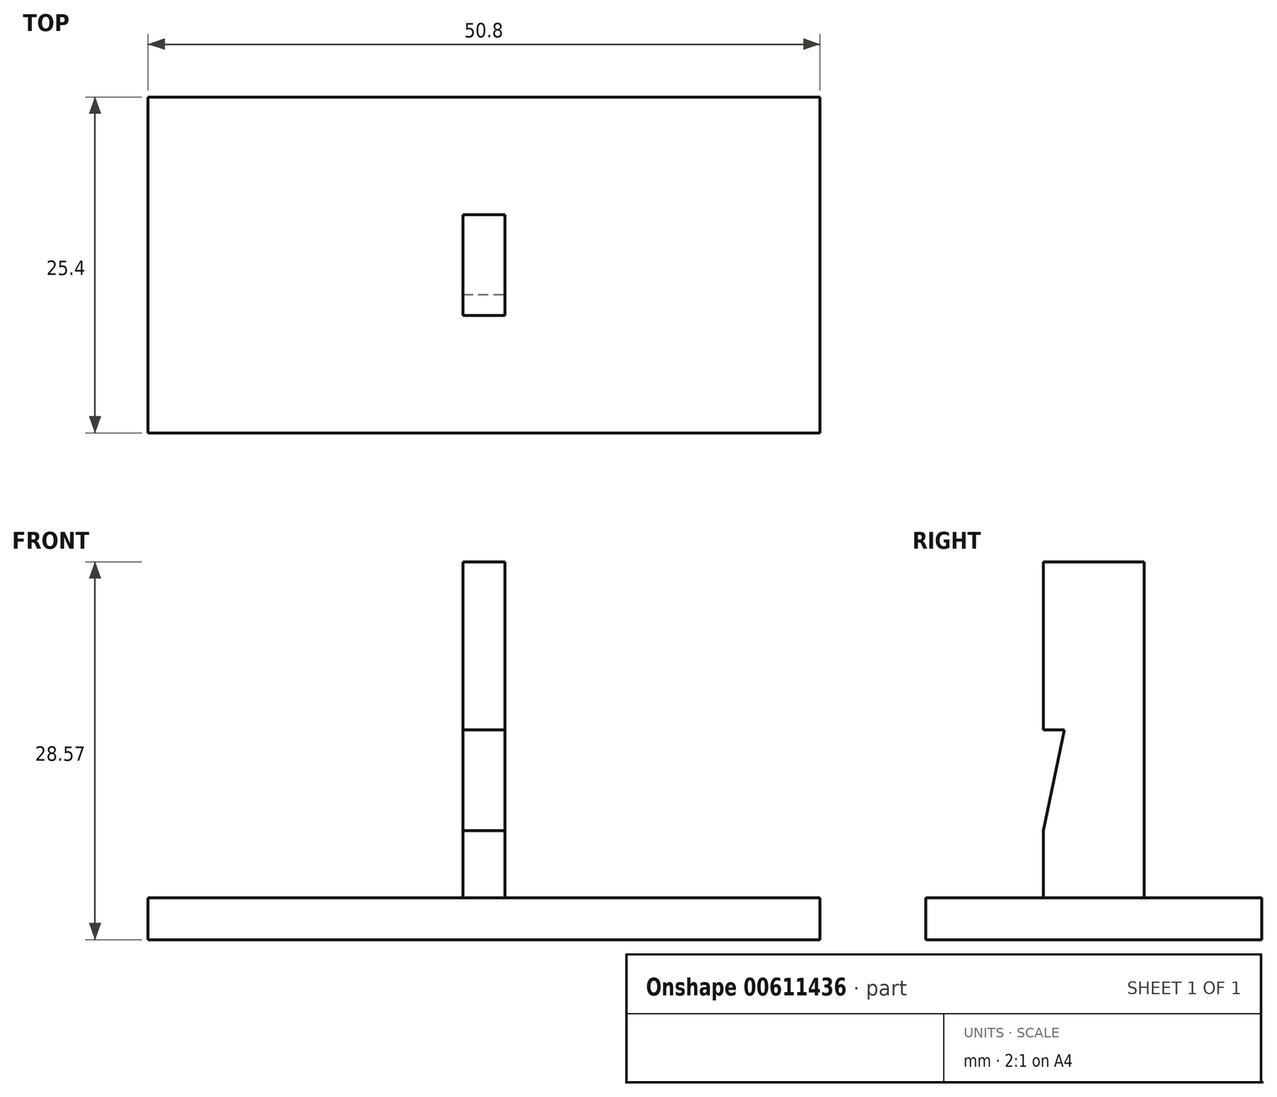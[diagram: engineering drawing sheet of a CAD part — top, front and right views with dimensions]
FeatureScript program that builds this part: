
annotation { "Feature Type Name" : "Feature", "Feature Type Description" : "" }
export const myFeature = defineFeature(function(context is Context, id is Id, definition is map)
    precondition{}
    {
        {
            var Q0;
            Q0=qCreatedBy(makeId("Top.planeOp"),FACE);
            var sketch = newSketch(context, id + "F0", { "sketchPlane" : qUnion([Q0])});
            skLineSegment(sketch, "E0.bottom", {"start": v(0, 0) * mm, "end": v(50.8, 0) * mm});
            skLineSegment(sketch, "E0.top", {"start": v(0, -25.4) * mm, "end": v(50.8, -25.4) * mm});
            skLineSegment(sketch, "E0.left", {"start": v(0, 0) * mm, "end": v(0, -25.4) * mm});
            skLineSegment(sketch, "E0.right", {"start": v(50.8, 0) * mm, "end": v(50.8, -25.4) * mm});
            skSolve(sketch);
        }
        {
            var Q0;
            Q0=makeQuery(id+"F0.imprint","IMPRINT",FACE,{"disambiguationData":[TD([[makeQuery(id+"F0.imprint","IMPRINT",EDGE,{"derivedFrom":sQuery(id+"F0.wireOp",EDGE,"E0.bottom")}),-1.0]])]});
            extrude(context, id + "F1", {"entities" : qUnion([Q0]), "depth" : 3.17 * mm, "offsetDistance" : 25.4 * mm});
        }
        {
            var Q0;
            Q0=makeQuery(id+"F1.opExtrude","CAP_FACE",FACE,{"disambiguationData":[OSD([sQuery(id+"F0.wireOp",EDGE,"E0.bottom"),sQuery(id+"F0.wireOp",EDGE,"E0.top"),sQuery(id+"F0.wireOp",EDGE,"E0.left"),sQuery(id+"F0.wireOp",EDGE,"E0.right")])],"isStart":false});
            var sketch = newSketch(context, id + "F2", { "sketchPlane" : qUnion([Q0])});
            skLineSegment(sketch, "E1", {"start": v(25.4, 0) * mm, "end": v(25.4, -25.4) * mm});
            skLineSegment(sketch, "E2", {"start": v(0, -12.7) * mm, "end": v(50.8, -12.7) * mm});
            skLineSegment(sketch, "E3", {"start": v(23.81, -12.7) * mm, "end": v(23.81, -16.51) * mm});
            skLineSegment(sketch, "E4", {"start": v(23.81, -16.51) * mm, "end": v(25.4, -16.51) * mm});
            skLineSegment(sketch, "E5.MirrorCS", {"start": v(23.81, -8.9) * mm, "end": v(25.4, -8.9) * mm});
            skLineSegment(sketch, "E6.MirrorCS", {"start": v(23.81, -12.7) * mm, "end": v(23.81, -8.9) * mm});
            skLineSegment(sketch, "E7.MirrorCS", {"start": v(26.99, -16.51) * mm, "end": v(25.4, -16.51) * mm});
            skLineSegment(sketch, "E8.MirrorCS", {"start": v(26.99, -12.7) * mm, "end": v(26.99, -16.51) * mm});
            skLineSegment(sketch, "E9.MirrorCS", {"start": v(26.99, -12.7) * mm, "end": v(26.99, -8.9) * mm});
            skLineSegment(sketch, "E10.MirrorCS", {"start": v(26.99, -8.9) * mm, "end": v(25.4, -8.9) * mm});
            skSolve(sketch);
        }
        {
            var Q0;
            {var subQ0=sQuery(id+"F2.wireOp",EDGE,"E7.MirrorCS");Q0=makeQuery(id+"F2.imprint","IMPRINT",FACE,{"disambiguationData":[TD([[makeQuery(id+"F2.imprint","IMPRINT",EDGE,{"derivedFrom":subQ0}),-1.0]])]});}
            var Q1;
            {var subQ4=sQuery(id+"F2.wireOp",EDGE,"E3");Q1=makeQuery(id+"F2.imprint","IMPRINT",FACE,{"disambiguationData":[TD([[makeQuery(id+"F2.imprint","IMPRINT",EDGE,{"derivedFrom":subQ4}),1.0]])]});}
            var Q2;
            {var subQ4=sQuery(id+"F2.wireOp",EDGE,"E9.MirrorCS");Q2=makeQuery(id+"F2.imprint","IMPRINT",FACE,{"disambiguationData":[TD([[makeQuery(id+"F2.imprint","IMPRINT",EDGE,{"derivedFrom":subQ4}),1.0]])]});}
            var Q3;
            {var subQ0=sQuery(id+"F2.wireOp",EDGE,"E5.MirrorCS");Q3=makeQuery(id+"F2.imprint","IMPRINT",FACE,{"disambiguationData":[TD([[makeQuery(id+"F2.imprint","IMPRINT",EDGE,{"derivedFrom":subQ0}),-1.0]])]});}
            extrude(context, id + "F3", {"entities" : qUnion([Q0, Q1, Q2, Q3]), "operationType" : NewBodyOperationType.ADD, "depth" : 25.4 * mm, "offsetDistance" : 25.4 * mm});
        }
        {
            var Q0;
            Q0=makeQuery(id+"F3.opExtrude","SWEPT_FACE",FACE,{"disambiguationData":[OSD([sQuery(id+"F2.wireOp",EDGE,"E8.MirrorCS"),sQuery(id+"F2.wireOp",EDGE,"E9.MirrorCS")])]});
            var sketch = newSketch(context, id + "F4", { "sketchPlane" : qUnion([Q0])});
            skLineSegment(sketch, "E11", {"start": v(-16.51, 15.88) * mm, "end": v(-14.92, 15.88) * mm});
            skLineSegment(sketch, "E12", {"start": v(-14.92, 15.88) * mm, "end": v(-16.51, 8.26) * mm});
            skLineSegment(sketch, "E13", {"start": v(-16.51, 15.88) * mm, "end": v(-16.51, 8.26) * mm});
            skSolve(sketch);
        }
        {
            var Q0;
            Q0=makeQuery(id+"F4.imprint","IMPRINT",FACE,{"disambiguationData":[TD([[makeQuery(id+"F4.imprint","IMPRINT",EDGE,{"derivedFrom":sQuery(id+"F4.wireOp",EDGE,"E11")}),-1.0]])]});
            extrude(context, id + "F5", {"entities" : qUnion([Q0]), "operationType" : NewBodyOperationType.REMOVE, "endBound" : BoundingType.UP_TO_NEXT, "oppositeDirection" : true, "depth" : 25.4 * mm, "offsetDistance" : 25.4 * mm});
        }
    });
